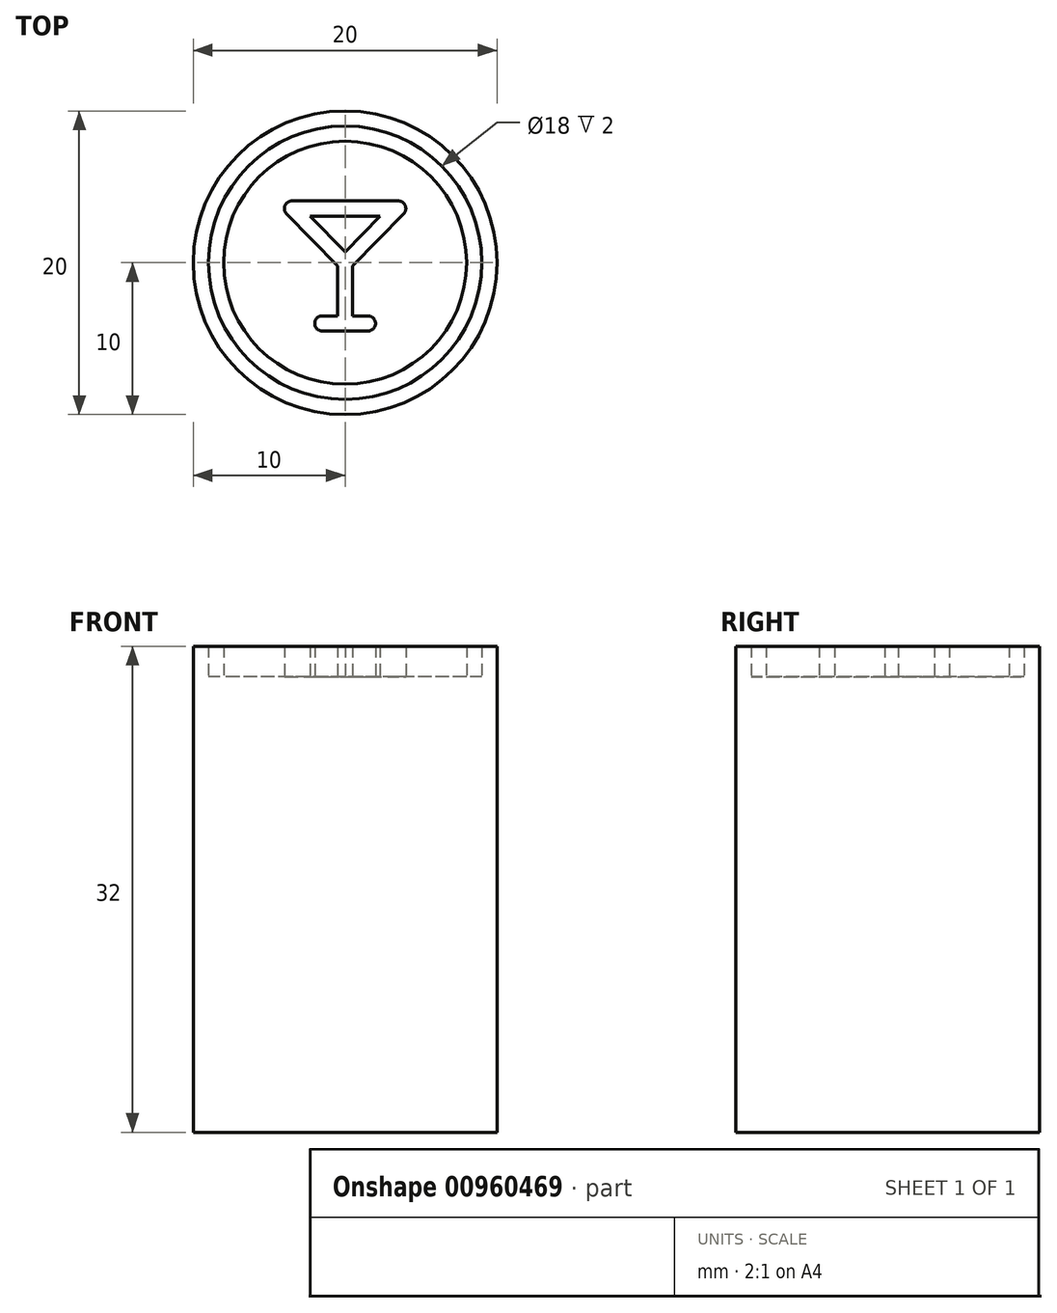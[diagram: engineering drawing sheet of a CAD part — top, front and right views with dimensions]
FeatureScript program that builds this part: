
annotation { "Feature Type Name" : "Feature", "Feature Type Description" : "" }
export const myFeature = defineFeature(function(context is Context, id is Id, definition is map)
    precondition{}
    {
        {
            var Q0;
            Q0=qCreatedBy(makeId("Top.planeOp"),FACE);
            var sketch = newSketch(context, id + "F0", { "sketchPlane" : qUnion([Q0])});
            skCircle(sketch, "E0", {"center": v(0, 0) * mm, "radius": 10 * mm});
            skSolve(sketch);
        }
        {
            var Q0;
            Q0=makeQuery(id+"F0.imprint","IMPRINT",FACE,{"disambiguationData":[TD([[makeQuery(id+"F0.imprint","IMPRINT",EDGE,{"derivedFrom":sQuery(id+"F0.wireOp",EDGE,"E0")}),1.0]])]});
            extrude(context, id + "F1", {"entities" : qUnion([Q0]), "depth" : 30 * mm, "offsetDistance" : 25 * mm});
        }
        {
            var Q0;
            Q0=makeQuery(id+"F1.opExtrude","CAP_FACE",FACE,{"disambiguationData":[OSD([sQuery(id+"F0.wireOp",EDGE,"E0")])],"isStart":false});
            var sketch = newSketch(context, id + "F2", { "sketchPlane" : qUnion([Q0])});
            skCircle(sketch, "E1", {"center": v(0, 0) * mm, "radius": 8 * mm});
            skCircle(sketch, "E2.0", {"center": v(0, 0) * mm, "radius": 9 * mm});
            skLineSegment(sketch, "E3", {"start": v(0, 0) * mm, "end": v(3.5, 3.57) * mm, "construction": true});
            skLineSegment(sketch, "E4", {"start": v(3.5, 3.57) * mm, "end": v(-3.5, 3.57) * mm, "construction": true});
            skLineSegment(sketch, "E5", {"start": v(-3.5, 3.57) * mm, "end": v(0, 0) * mm, "construction": true});
            skLineSegment(sketch, "E6", {"start": v(0, 0) * mm, "end": v(0, -4) * mm, "construction": true});
            skLineSegment(sketch, "E7", {"start": v(-1.5, -4) * mm, "end": v(1.5, -4) * mm, "construction": true});
            skArc(sketch, "E8.0.startCap", {"start": v(3.5, 4.07) * mm, "mid": v(4, 3.57) * mm, "end": v(3.5, 3.07) * mm});
            skArc(sketch, "E8.0.endCap", {"start": v(-3.5, 3.07) * mm, "mid": v(-4, 3.57) * mm, "end": v(-3.5, 4.07) * mm});
            skLineSegment(sketch, "E8.0.left", {"start": v(3.5, 3.07) * mm, "end": v(-3.5, 3.07) * mm});
            skLineSegment(sketch, "E8.0.right", {"start": v(3.5, 4.07) * mm, "end": v(-3.5, 4.07) * mm});
            skArc(sketch, "E8.1.startCap", {"start": v(-3.86, 3.22) * mm, "mid": v(-3.85, 3.93) * mm, "end": v(-3.14, 3.92) * mm});
            skArc(sketch, "E8.1.endCap", {"start": v(0.36, 0.35) * mm, "mid": v(0.35, -0.36) * mm, "end": v(-0.36, -0.35) * mm});
            skLineSegment(sketch, "E8.1.left", {"start": v(-3.14, 3.92) * mm, "end": v(0.36, 0.35) * mm});
            skLineSegment(sketch, "E8.1.right", {"start": v(-3.86, 3.22) * mm, "end": v(-0.36, -0.35) * mm});
            skArc(sketch, "E8.2.startCap", {"start": v(0.36, -0.35) * mm, "mid": v(-0.35, -0.36) * mm, "end": v(-0.36, 0.35) * mm});
            skArc(sketch, "E8.2.endCap", {"start": v(3.14, 3.92) * mm, "mid": v(3.85, 3.93) * mm, "end": v(3.86, 3.22) * mm});
            skLineSegment(sketch, "E8.2.left", {"start": v(-0.36, 0.35) * mm, "end": v(3.14, 3.92) * mm});
            skLineSegment(sketch, "E8.2.right", {"start": v(0.36, -0.35) * mm, "end": v(3.86, 3.22) * mm});
            skArc(sketch, "E8.3.startCap", {"start": v(-0.5, 0) * mm, "mid": v(0, 0.5) * mm, "end": v(0.5, 0) * mm});
            skArc(sketch, "E8.3.endCap", {"start": v(0.5, -4) * mm, "mid": v(0, -4.5) * mm, "end": v(-0.5, -4) * mm});
            skLineSegment(sketch, "E8.3.left", {"start": v(0.5, 0) * mm, "end": v(0.5, -4) * mm});
            skLineSegment(sketch, "E8.3.right", {"start": v(-0.5, 0) * mm, "end": v(-0.5, -4) * mm});
            skArc(sketch, "E8.4.startCap", {"start": v(-1.5, -4.5) * mm, "mid": v(-2, -4) * mm, "end": v(-1.5, -3.5) * mm});
            skArc(sketch, "E8.4.endCap", {"start": v(1.5, -3.5) * mm, "mid": v(2, -4) * mm, "end": v(1.5, -4.5) * mm});
            skLineSegment(sketch, "E8.4.left", {"start": v(-1.5, -3.5) * mm, "end": v(1.5, -3.5) * mm});
            skLineSegment(sketch, "E8.4.right", {"start": v(-1.5, -4.5) * mm, "end": v(1.5, -4.5) * mm});
            skSolve(sketch);
        }
        {
            var Q0;
            Q0=makeQuery(id+"F2.imprint","IMPRINT",FACE,{"disambiguationData":[TD([[makeQuery(id+"F2.imprint","IMPRINT",EDGE,{"derivedFrom":sQuery(id+"F2.wireOp",EDGE,"E1")}),1.0]])]});
            var Q1;
            Q1=makeQuery(id+"F2.imprint","IMPRINT",FACE,{"disambiguationData":[TD([[makeQuery(id+"F2.imprint","IMPRINT",EDGE,{"derivedFrom":sQuery(id+"F2.wireOp",EDGE,"E2.0")}),-1.0]])]});
            var Q2;
            {var subQ0=sQuery(id+"F2.wireOp",EDGE,"E8.2.left");var subQ1=sQuery(id+"F2.wireOp",EDGE,"E8.0.left");var subQ2=makeQuery(id+"F2.imprint","INTERSECT",VERTEX,{"derivedFrom":[subQ1,subQ0]});Q2=makeQuery(id+"F2.imprint","IMPRINT",FACE,{"disambiguationData":[TD([[makeQuery(id+"F2.imprint","IMPRINT",EDGE,{"disambiguationData":[TD([[subQ2,-1.0]])],"derivedFrom":subQ1}),1.0]])]});}
            extrude(context, id + "F3", {"entities" : qUnion([Q0, Q1, Q2]), "operationType" : NewBodyOperationType.ADD, "depth" : 2 * mm, "offsetDistance" : 25 * mm});
        }
    });
